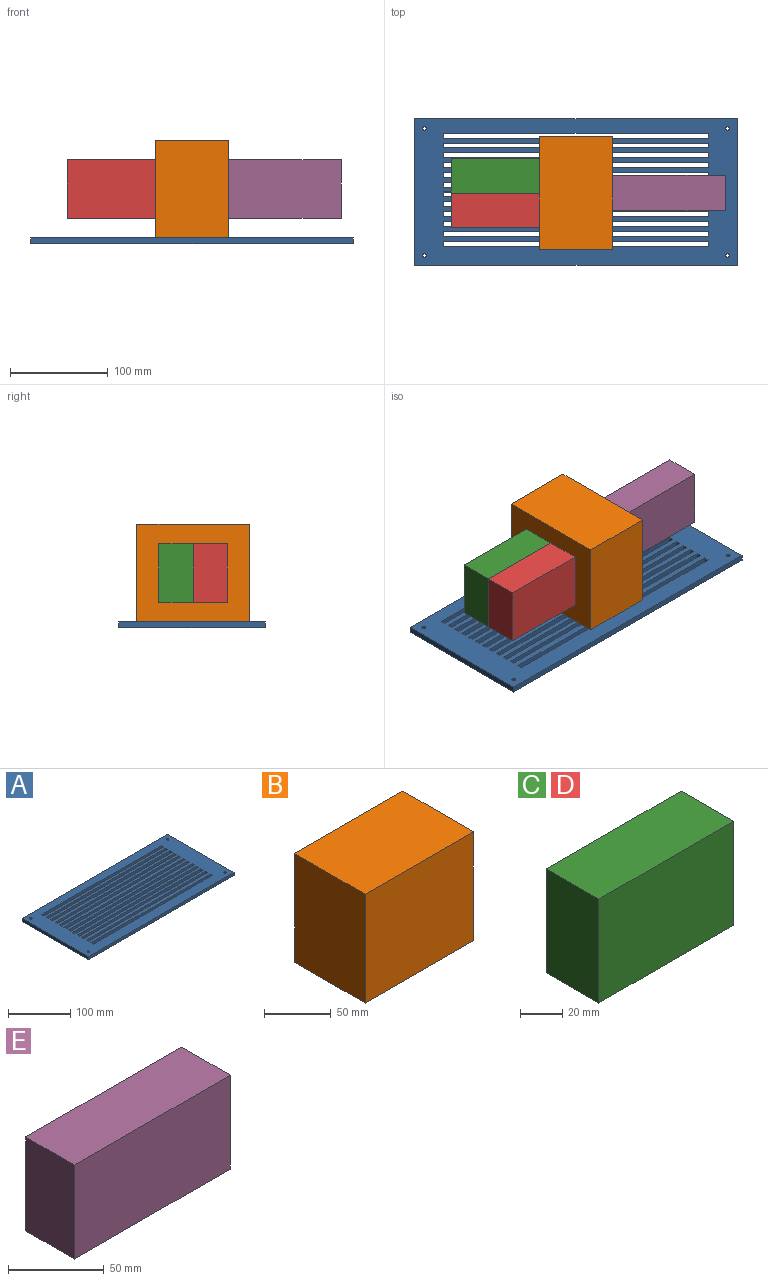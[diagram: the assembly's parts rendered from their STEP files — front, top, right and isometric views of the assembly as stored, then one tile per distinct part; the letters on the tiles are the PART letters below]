
ASSEMBLY  parts=5 mates=4
PART A: 58 faces, bbox 330x150x6 mm
  f0: plane 330x150mm, normal (0,0,1), area 33254.6mm2, adj f2,f3,f4,f5,f6,f7,f8,f9
  f1: plane 330x150mm, normal (0,0,-1), area 33254.6mm2, adj f2,f3,f4,f5,f6,f7,f8,f9
  f2: plane 330x6mm, normal (0,1,0), area 1980mm2, adj f0,f1,f3,f5
  f3: plane 150x6mm, normal (-1,0,0), area 900mm2, adj f0,f1,f2,f4
  f4: plane 330x6mm, normal (0,-1,0), area 1980mm2, adj f0,f1,f3,f5
  f5: plane 150x6mm, normal (1,0,0), area 900mm2, adj f0,f1,f2,f4
  f6: cylinder r=1.9mm len=6mm, axis (0,0,1), area 71.6mm2, adj f0,f1
  f7: cylinder r=1.9mm len=6mm, axis (0,0,1), area 71.6mm2, adj f0,f1
  f8: cylinder r=1.9mm len=6mm, axis (0,0,1), area 71.6mm2, adj f0,f1
  f9: cylinder r=1.9mm len=6mm, axis (0,0,1), area 71.6mm2, adj f0,f1
  f10: plane 6x5mm, normal (1,0,0), area 30mm2, adj f0,f1,f11,f12
  f11: plane 270x6mm, normal (0,-1,0), area 1620mm2, adj f0,f1,f10,f13
  f12: plane 270x6mm, normal (0,1,0), area 1620mm2, adj f0,f1,f10,f13
  f13: plane 6x5mm, normal (-1,0,0), area 30mm2, adj f0,f1,f11,f12
  f14: plane 6x5mm, normal (1,0,0), area 30mm2, adj f0,f1,f15,f16
  f15: plane 270x6mm, normal (0,-1,0), area 1620mm2, adj f0,f1,f14,f17
  f16: plane 270x6mm, normal (0,1,0), area 1620mm2, adj f0,f1,f14,f17
  f17: plane 6x5mm, normal (-1,0,0), area 30mm2, adj f0,f1,f15,f16
  f18: plane 6x5mm, normal (1,0,0), area 30mm2, adj f0,f1,f19,f20
  f19: plane 270x6mm, normal (0,-1,0), area 1620mm2, adj f0,f1,f18,f21
  f20: plane 270x6mm, normal (0,1,0), area 1620mm2, adj f0,f1,f18,f21
  f21: plane 6x5mm, normal (-1,0,0), area 30mm2, adj f0,f1,f19,f20
  f22: plane 6x5mm, normal (1,0,0), area 30mm2, adj f0,f1,f23,f24
  f23: plane 270x6mm, normal (0,-1,0), area 1620mm2, adj f0,f1,f22,f25
  f24: plane 270x6mm, normal (0,1,0), area 1620mm2, adj f0,f1,f22,f25
  f25: plane 6x5mm, normal (-1,0,0), area 30mm2, adj f0,f1,f23,f24
  f26: plane 6x5mm, normal (1,0,0), area 30mm2, adj f0,f1,f27,f28
  f27: plane 270x6mm, normal (0,-1,0), area 1620mm2, adj f0,f1,f26,f29
  f28: plane 270x6mm, normal (0,1,0), area 1620mm2, adj f0,f1,f26,f29
  f29: plane 6x5mm, normal (-1,0,0), area 30mm2, adj f0,f1,f27,f28
  f30: plane 6x5mm, normal (1,0,0), area 30mm2, adj f0,f1,f31,f32
  f31: plane 270x6mm, normal (0,-1,0), area 1620mm2, adj f0,f1,f30,f33
  f32: plane 270x6mm, normal (0,1,0), area 1620mm2, adj f0,f1,f30,f33
  f33: plane 6x5mm, normal (-1,0,0), area 30mm2, adj f0,f1,f31,f32
  f34: plane 6x5mm, normal (1,0,0), area 30mm2, adj f0,f1,f35,f36
  f35: plane 270x6mm, normal (0,-1,0), area 1620mm2, adj f0,f1,f34,f37
  f36: plane 270x6mm, normal (0,1,0), area 1620mm2, adj f0,f1,f34,f37
  f37: plane 6x5mm, normal (-1,0,0), area 30mm2, adj f0,f1,f35,f36
  f38: plane 6x5mm, normal (1,0,0), area 30mm2, adj f0,f1,f39,f40
  f39: plane 270x6mm, normal (0,-1,0), area 1620mm2, adj f0,f1,f38,f41
  f40: plane 270x6mm, normal (0,1,0), area 1620mm2, adj f0,f1,f38,f41
  f41: plane 6x5mm, normal (-1,0,0), area 30mm2, adj f0,f1,f39,f40
  f42: plane 6x5mm, normal (1,0,0), area 30mm2, adj f0,f1,f43,f44
  f43: plane 270x6mm, normal (0,-1,0), area 1620mm2, adj f0,f1,f42,f45
  f44: plane 270x6mm, normal (0,1,0), area 1620mm2, adj f0,f1,f42,f45
  f45: plane 6x5mm, normal (-1,0,0), area 30mm2, adj f0,f1,f43,f44
  f46: plane 6x5mm, normal (1,0,0), area 30mm2, adj f0,f1,f47,f48
  f47: plane 270x6mm, normal (0,-1,0), area 1620mm2, adj f0,f1,f46,f49
  f48: plane 270x6mm, normal (0,1,0), area 1620mm2, adj f0,f1,f46,f49
  f49: plane 6x5mm, normal (-1,0,0), area 30mm2, adj f0,f1,f47,f48
  f50: plane 6x5mm, normal (1,0,0), area 30mm2, adj f0,f1,f51,f52
  f51: plane 270x6mm, normal (0,-1,0), area 1620mm2, adj f0,f1,f50,f53
  f52: plane 270x6mm, normal (0,1,0), area 1620mm2, adj f0,f1,f50,f53
  f53: plane 6x5mm, normal (-1,0,0), area 30mm2, adj f0,f1,f51,f52
  f54: plane 6x5mm, normal (1,0,0), area 30mm2, adj f0,f1,f55,f56
  f55: plane 270x6mm, normal (0,-1,0), area 1620mm2, adj f0,f1,f54,f57
  f56: plane 270x6mm, normal (0,1,0), area 1620mm2, adj f0,f1,f54,f57
  f57: plane 6x5mm, normal (-1,0,0), area 30mm2, adj f0,f1,f55,f56
PART B: 6 faces, bbox 115x75x100 mm
  f0: plane 115x100mm, normal (0,1,0), area 11500mm2, adj f1,f3,f4,f5
  f1: plane 100x75mm, normal (-1,0,0), area 7500mm2, adj f0,f2,f4,f5
  f2: plane 115x100mm, normal (0,-1,0), area 11500mm2, adj f1,f3,f4,f5
  f3: plane 100x75mm, normal (1,0,0), area 7500mm2, adj f0,f2,f4,f5
  f4: plane 115x75mm, normal (0,0,1), area 8625mm2, adj f0,f1,f2,f3
  f5: plane 115x75mm, normal (0,0,-1), area 8625mm2, adj f0,f1,f2,f3
PART C: 6 faces, bbox 90x35x60 mm
  f0: plane 60x35mm, normal (1,0,0), area 2100mm2, adj f1,f3,f4,f5
  f1: plane 90x60mm, normal (0,1,0), area 5400mm2, adj f0,f2,f4,f5
  f2: plane 60x35mm, normal (-1,0,0), area 2100mm2, adj f1,f3,f4,f5
  f3: plane 90x60mm, normal (0,-1,0), area 5400mm2, adj f0,f2,f4,f5
  f4: plane 90x35mm, normal (0,0,1), area 3150mm2, adj f0,f1,f2,f3
  f5: plane 90x35mm, normal (0,0,-1), area 3150mm2, adj f0,f1,f2,f3
PART D: same geometry as C
PART E: 6 faces, bbox 115x36x60 mm
  f0: plane 115x60mm, normal (0,1,0), area 6900mm2, adj f1,f3,f4,f5
  f1: plane 60x36mm, normal (-1,0,0), area 2160mm2, adj f0,f2,f4,f5
  f2: plane 115x60mm, normal (0,-1,0), area 6900mm2, adj f1,f3,f4,f5
  f3: plane 60x36mm, normal (1,0,0), area 2160mm2, adj f0,f2,f4,f5
  f4: plane 115x36mm, normal (0,0,1), area 4140mm2, adj f0,f1,f2,f3
  f5: plane 115x36mm, normal (0,0,-1), area 4140mm2, adj f0,f1,f2,f3
PLACE A t=(0,1.18,-6)mm
PLACE B rot(axis=(-0.71,-0.71,0),180deg) t=(0.62,3.66,100)mm
PLACE C rot(axis=(0,-1,0),180deg) t=(-55.76,5.97,80)mm
PLACE D rot(axis=(0,-1,0),180deg) t=(-55.76,-29.03,80)mm
PLACE E rot(axis=(0,-1,0),180deg) t=(68.9,5,80)mm
MATE fastened B.f0 <-> E.f3  axis (1,0,0) through (37.5,0,50)mm
MATE fastened C.f2 <-> B.f2  axis (1,0,0) through (-37.5,0,50)mm
MATE fastened B.f4 <-> A.f0  axis (0,0,-1) through (0,0,0)mm
MATE fastened C.f3 <-> D.f1  axis (0,-1,0) through (-82.5,0,50)mm
